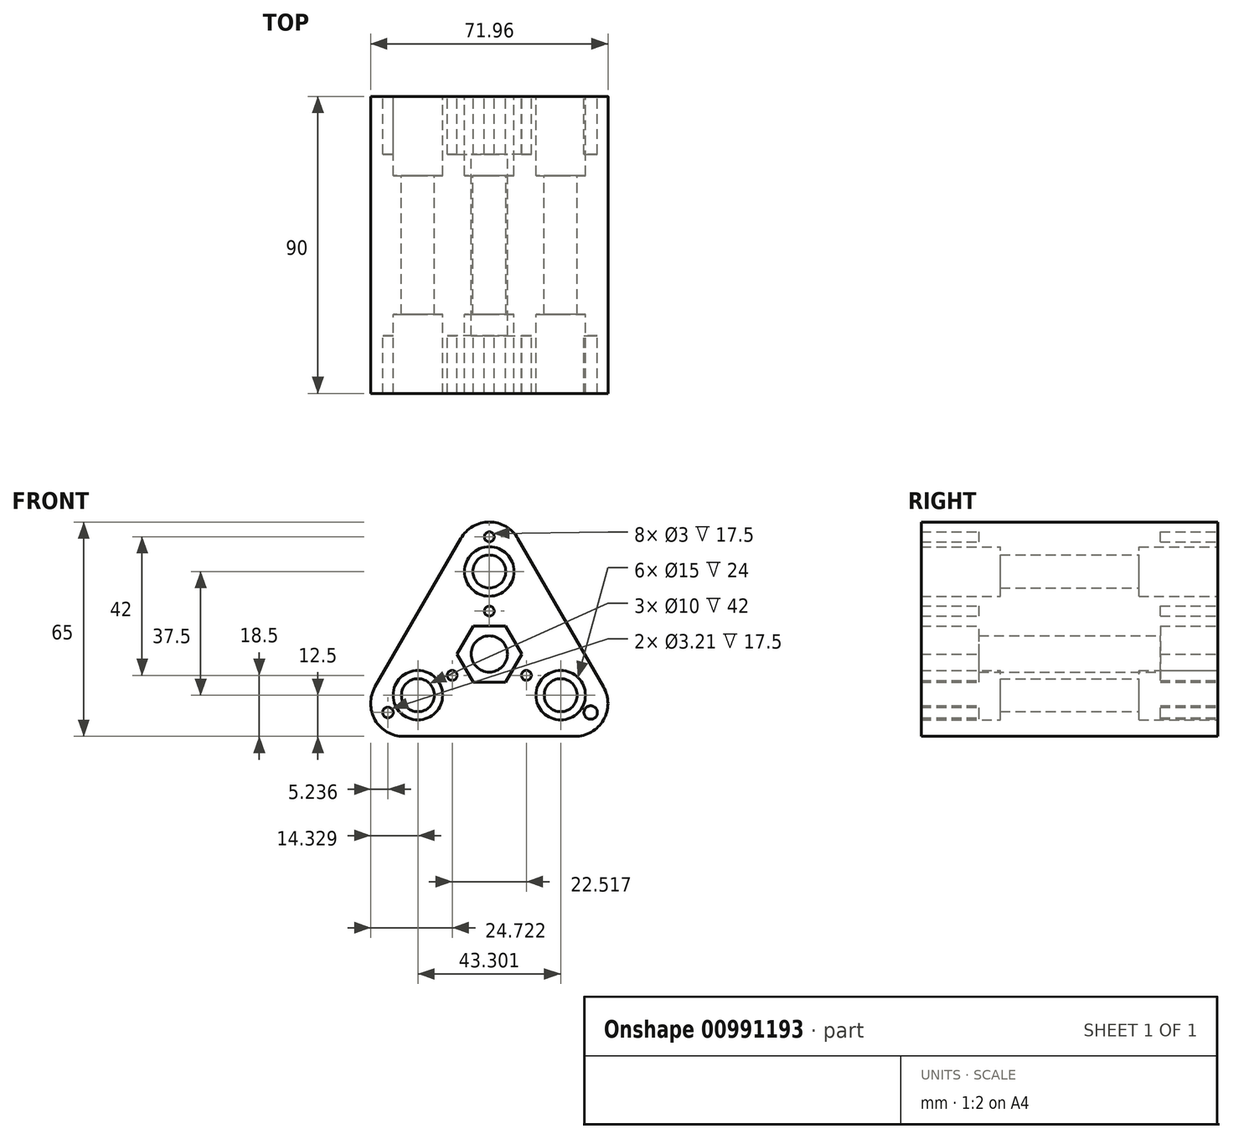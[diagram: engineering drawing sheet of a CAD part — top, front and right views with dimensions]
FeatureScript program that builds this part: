
annotation { "Feature Type Name" : "Feature", "Feature Type Description" : "" }
export const myFeature = defineFeature(function(context is Context, id is Id, definition is map)
    precondition{}
    {
        {
            var Q0;
            Q0=qCreatedBy(makeId("Front.planeOp"),FACE);
            var sketch = newSketch(context, id + "F0", { "sketchPlane" : qUnion([Q0])});
            skCircle(sketch, "E0", {"center": v(0, 0) * mm, "radius": 25 * mm, "construction": true});
            skLineSegment(sketch, "E1.0", {"start": v(0, 25) * mm, "end": v(21.65, -12.5) * mm, "construction": true});
            skLineSegment(sketch, "E1.1", {"start": v(21.65, -12.5) * mm, "end": v(-21.65, -12.5) * mm, "construction": true});
            skLineSegment(sketch, "E1.2", {"start": v(-21.65, -12.5) * mm, "end": v(0, 25) * mm, "construction": true});
            skCircle(sketch, "E2", {"center": v(0, 25) * mm, "radius": 7.5 * mm});
            skCircle(sketch, "E3", {"center": v(21.65, -12.5) * mm, "radius": 7.5 * mm});
            skCircle(sketch, "E4", {"center": v(-21.65, -12.5) * mm, "radius": 7.5 * mm});
            skCircle(sketch, "E5", {"center": v(0, 0) * mm, "radius": 9.81 * mm, "construction": true});
            skCircle(sketch, "E6", {"center": v(-21.65, -12.5) * mm, "radius": 5 * mm});
            skCircle(sketch, "E7", {"center": v(0, 25) * mm, "radius": 5 * mm});
            skCircle(sketch, "E8", {"center": v(21.65, -12.5) * mm, "radius": 5 * mm});
            skLineSegment(sketch, "E9.0", {"start": v(-9.81, 0) * mm, "end": v(-4.9, 8.5) * mm});
            skLineSegment(sketch, "E9.1", {"start": v(-4.9, 8.5) * mm, "end": v(4.9, 8.5) * mm});
            skLineSegment(sketch, "E9.2", {"start": v(4.9, 8.5) * mm, "end": v(9.82, 0) * mm});
            skLineSegment(sketch, "E9.3", {"start": v(9.81, 0) * mm, "end": v(4.9, -8.5) * mm});
            skLineSegment(sketch, "E9.4", {"start": v(4.9, -8.5) * mm, "end": v(-4.9, -8.5) * mm});
            skLineSegment(sketch, "E9.5", {"start": v(-4.9, -8.5) * mm, "end": v(-9.81, 0) * mm});
            skLineSegment(sketch, "E10.0", {"start": v(25.98, -25) * mm, "end": v(-25.98, -25) * mm});
            skLineSegment(sketch, "E10.1", {"start": v(-34.64, -10) * mm, "end": v(-8.66, 35) * mm});
            skLineSegment(sketch, "E10.2", {"start": v(8.66, 35) * mm, "end": v(34.64, -10) * mm});
            skPoint(sketch, "E10.0.midPoint", {"position": v(0, -25) * mm});
            skPoint(sketch, "E11.visualSharp", {"position": v(0, 50) * mm});
            skArc(sketch, "E11.filletArc", {"start": v(8.66, 35) * mm, "mid": v(0, 40) * mm, "end": v(-8.66, 35) * mm});
            skPoint(sketch, "E12.visualSharp", {"position": v(43.3, -25) * mm});
            skArc(sketch, "E12.filletArc", {"start": v(25.98, -25) * mm, "mid": v(34.64, -20) * mm, "end": v(34.64, -10) * mm});
            skPoint(sketch, "E13.visualSharp", {"position": v(-43.3, -25) * mm});
            skArc(sketch, "E13.filletArc", {"start": v(-34.64, -10) * mm, "mid": v(-34.64, -20) * mm, "end": v(-25.98, -25) * mm});
            skCircle(sketch, "E14", {"center": v(0, 0) * mm, "radius": 5.5 * mm});
            skPoint(sketch, "E15.0.midPoint", {"position": v(0, -10) * mm});
            skPoint(sketch, "E16.visualSharp", {"position": v(17.32, -10) * mm});
            skPoint(sketch, "E17.visualSharp", {"position": v(-17.32, -10) * mm});
            skPoint(sketch, "E18.visualSharp", {"position": v(0, 20) * mm});
            skCircle(sketch, "E19", {"center": v(11.26, -6.5) * mm, "radius": 1.5 * mm});
            skCircle(sketch, "E20", {"center": v(-11.26, -6.5) * mm, "radius": 1.5 * mm});
            skCircle(sketch, "E21", {"center": v(0, 13) * mm, "radius": 1.5 * mm});
            skCircle(sketch, "E22", {"center": v(-30.74, -17.75) * mm, "radius": 1.6 * mm});
            skCircle(sketch, "E23", {"center": v(-30.74, -17.75) * mm, "radius": 3 * mm});
            skLineSegment(sketch, "E24", {"start": v(34.64, -20) * mm, "end": v(21.65, -12.5) * mm, "construction": true});
            skCircle(sketch, "E25", {"center": v(30.74, -17.75) * mm, "radius": 2.03 * mm});
            skCircle(sketch, "E26", {"center": v(30.74, -17.75) * mm, "radius": 3 * mm});
            skCircle(sketch, "E27", {"center": v(11.26, -6.5) * mm, "radius": 3 * mm});
            skCircle(sketch, "E28", {"center": v(-11.26, -6.5) * mm, "radius": 3 * mm});
            skCircle(sketch, "E29", {"center": v(0, 13) * mm, "radius": 3 * mm});
            skCircle(sketch, "E30", {"center": v(0, 35.5) * mm, "radius": 1.5 * mm});
            skCircle(sketch, "E31", {"center": v(0, 35.5) * mm, "radius": 3 * mm});
            skLineSegment(sketch, "E32", {"start": v(-21.65, -12.5) * mm, "end": v(0, 0) * mm, "construction": true});
            skLineSegment(sketch, "E33", {"start": v(0, 0) * mm, "end": v(21.65, -12.5) * mm, "construction": true});
            skLineSegment(sketch, "E34", {"start": v(0, 0) * mm, "end": v(0, 25) * mm, "construction": true});
            skLineSegment(sketch, "E35", {"start": v(0, 40) * mm, "end": v(0, 25) * mm, "construction": true});
            skLineSegment(sketch, "E36", {"start": v(-34.64, -20) * mm, "end": v(-21.65, -12.5) * mm, "construction": true});
            skSolve(sketch);
        }
        {
            var Q0;
            Q0=makeQuery(id+"F0.imprint","IMPRINT",FACE,{"disambiguationData":[TD([[makeQuery(id+"F0.imprint","IMPRINT",EDGE,{"derivedFrom":sQuery(id+"F0.wireOp",EDGE,"E2")}),-1.0]])]});
            var Q1;
            Q1=makeQuery(id+"F0.imprint","IMPRINT",FACE,{"disambiguationData":[TD([[makeQuery(id+"F0.imprint","IMPRINT",EDGE,{"derivedFrom":sQuery(id+"F0.wireOp",EDGE,"E9.0")}),-1.0]])]});
            var Q2;
            Q2=makeQuery(id+"F0.imprint","IMPRINT",FACE,{"disambiguationData":[TD([[makeQuery(id+"F0.imprint","IMPRINT",EDGE,{"derivedFrom":sQuery(id+"F0.wireOp",EDGE,"E4")}),1.0]])]});
            var Q3;
            Q3=makeQuery(id+"F0.imprint","IMPRINT",FACE,{"disambiguationData":[TD([[makeQuery(id+"F0.imprint","IMPRINT",EDGE,{"derivedFrom":sQuery(id+"F0.wireOp",EDGE,"E3")}),1.0]])]});
            var Q4;
            Q4=makeQuery(id+"F0.imprint","IMPRINT",FACE,{"disambiguationData":[TD([[makeQuery(id+"F0.imprint","IMPRINT",EDGE,{"derivedFrom":sQuery(id+"F0.wireOp",EDGE,"E2")}),1.0]])]});
            var Q5;
            Q5=makeQuery(id+"F0.imprint","IMPRINT",FACE,{"disambiguationData":[TD([[makeQuery(id+"F0.imprint","IMPRINT",EDGE,{"derivedFrom":sQuery(id+"F0.wireOp",EDGE,"E9.0")}),1.0]])]});
            var Q6;
            Q6=makeQuery(id+"F0.imprint","IMPRINT",FACE,{"disambiguationData":[TD([[makeQuery(id+"F0.imprint","IMPRINT",EDGE,{"derivedFrom":sQuery(id+"F0.wireOp",EDGE,"E21")}),1.0]])]});
            var Q7;
            Q7=makeQuery(id+"F0.imprint","IMPRINT",FACE,{"disambiguationData":[TD([[makeQuery(id+"F0.imprint","IMPRINT",EDGE,{"derivedFrom":sQuery(id+"F0.wireOp",EDGE,"E20")}),1.0]])]});
            var Q8;
            Q8=makeQuery(id+"F0.imprint","IMPRINT",FACE,{"disambiguationData":[TD([[makeQuery(id+"F0.imprint","IMPRINT",EDGE,{"derivedFrom":sQuery(id+"F0.wireOp",EDGE,"E19")}),1.0]])]});
            var Q9;
            Q9=makeQuery(id+"F0.imprint","IMPRINT",FACE,{"disambiguationData":[TD([[makeQuery(id+"F0.imprint","IMPRINT",EDGE,{"derivedFrom":sQuery(id+"F0.wireOp",EDGE,"E21")}),-1.0]])]});
            var Q10;
            Q10=makeQuery(id+"F0.imprint","IMPRINT",FACE,{"disambiguationData":[TD([[makeQuery(id+"F0.imprint","IMPRINT",EDGE,{"derivedFrom":sQuery(id+"F0.wireOp",EDGE,"E20")}),-1.0]])]});
            var Q11;
            Q11=makeQuery(id+"F0.imprint","IMPRINT",FACE,{"disambiguationData":[TD([[makeQuery(id+"F0.imprint","IMPRINT",EDGE,{"derivedFrom":sQuery(id+"F0.wireOp",EDGE,"E19")}),-1.0]])]});
            extrude(context, id + "F1", {"entities" : qUnion([Q0, Q1, Q2, Q3, Q4, Q5, Q6, Q7, Q8, Q9, Q10, Q11]), "depth" : 42 * mm, "offsetDistance" : 25 * mm, "symmetric" : true});
        }
        {
            var Q0;
            Q0=makeQuery(id+"F0.imprint","IMPRINT",FACE,{"disambiguationData":[TD([[makeQuery(id+"F0.imprint","IMPRINT",EDGE,{"derivedFrom":sQuery(id+"F0.wireOp",EDGE,"E2")}),-1.0]])]});
            var Q1;
            Q1=makeQuery(id+"F0.imprint","IMPRINT",FACE,{"disambiguationData":[TD([[makeQuery(id+"F0.imprint","IMPRINT",EDGE,{"derivedFrom":sQuery(id+"F0.wireOp",EDGE,"E25")}),-1.0]])]});
            var Q2;
            Q2=makeQuery(id+"F0.imprint","IMPRINT",FACE,{"disambiguationData":[TD([[makeQuery(id+"F0.imprint","IMPRINT",EDGE,{"derivedFrom":sQuery(id+"F0.wireOp",EDGE,"E22")}),-1.0]])]});
            var Q3;
            Q3=makeQuery(id+"F0.imprint","IMPRINT",FACE,{"disambiguationData":[TD([[makeQuery(id+"F0.imprint","IMPRINT",EDGE,{"derivedFrom":sQuery(id+"F0.wireOp",EDGE,"E30")}),-1.0]])]});
            var Q4;
            Q4=makeQuery(id+"F0.imprint","IMPRINT",FACE,{"disambiguationData":[TD([[makeQuery(id+"F0.imprint","IMPRINT",EDGE,{"derivedFrom":sQuery(id+"F0.wireOp",EDGE,"E21")}),-1.0]])]});
            var Q5;
            Q5=makeQuery(id+"F0.imprint","IMPRINT",FACE,{"disambiguationData":[TD([[makeQuery(id+"F0.imprint","IMPRINT",EDGE,{"derivedFrom":sQuery(id+"F0.wireOp",EDGE,"E21")}),1.0]])]});
            var Q6;
            Q6=makeQuery(id+"F0.imprint","IMPRINT",FACE,{"disambiguationData":[TD([[makeQuery(id+"F0.imprint","IMPRINT",EDGE,{"derivedFrom":sQuery(id+"F0.wireOp",EDGE,"E19")}),-1.0]])]});
            var Q7;
            Q7=makeQuery(id+"F0.imprint","IMPRINT",FACE,{"disambiguationData":[TD([[makeQuery(id+"F0.imprint","IMPRINT",EDGE,{"derivedFrom":sQuery(id+"F0.wireOp",EDGE,"E19")}),1.0]])]});
            var Q8;
            Q8=makeQuery(id+"F0.imprint","IMPRINT",FACE,{"disambiguationData":[TD([[makeQuery(id+"F0.imprint","IMPRINT",EDGE,{"derivedFrom":sQuery(id+"F0.wireOp",EDGE,"E20")}),-1.0]])]});
            var Q9;
            Q9=makeQuery(id+"F0.imprint","IMPRINT",FACE,{"disambiguationData":[TD([[makeQuery(id+"F0.imprint","IMPRINT",EDGE,{"derivedFrom":sQuery(id+"F0.wireOp",EDGE,"E20")}),1.0]])]});
            var Q10;
            Q10=makeQuery(id+"F0.imprint","IMPRINT",FACE,{"disambiguationData":[TD([[makeQuery(id+"F0.imprint","IMPRINT",EDGE,{"derivedFrom":sQuery(id+"F0.wireOp",EDGE,"E9.0")}),-1.0]])]});
            var Q11;
            Q11=makeQuery(id+"F0.imprint","IMPRINT",FACE,{"disambiguationData":[TD([[makeQuery(id+"F0.imprint","IMPRINT",EDGE,{"derivedFrom":sQuery(id+"F0.wireOp",EDGE,"E30")}),1.0]])]});
            var Q12;
            Q12=makeQuery(id+"F0.imprint","IMPRINT",FACE,{"disambiguationData":[TD([[makeQuery(id+"F0.imprint","IMPRINT",EDGE,{"derivedFrom":sQuery(id+"F0.wireOp",EDGE,"E25")}),1.0]])]});
            var Q13;
            Q13=makeQuery(id+"F0.imprint","IMPRINT",FACE,{"disambiguationData":[TD([[makeQuery(id+"F0.imprint","IMPRINT",EDGE,{"derivedFrom":sQuery(id+"F0.wireOp",EDGE,"E22")}),1.0]])]});
            extrude(context, id + "F2", {"entities" : qUnion([Q0, Q1, Q2, Q3, Q4, Q5, Q6, Q7, Q8, Q9, Q10, Q11, Q12, Q13]), "operationType" : NewBodyOperationType.ADD, "depth" : 55 * mm, "offsetDistance" : 25 * mm, "symmetric" : true});
        }
        {
            var Q0;
            Q0=makeQuery(id+"F0.imprint","IMPRINT",FACE,{"disambiguationData":[TD([[makeQuery(id+"F0.imprint","IMPRINT",EDGE,{"derivedFrom":sQuery(id+"F0.wireOp",EDGE,"E2")}),-1.0]])]});
            var Q1;
            Q1=makeQuery(id+"F0.imprint","IMPRINT",FACE,{"disambiguationData":[TD([[makeQuery(id+"F0.imprint","IMPRINT",EDGE,{"derivedFrom":sQuery(id+"F0.wireOp",EDGE,"E25")}),-1.0]])]});
            var Q2;
            Q2=makeQuery(id+"F0.imprint","IMPRINT",FACE,{"disambiguationData":[TD([[makeQuery(id+"F0.imprint","IMPRINT",EDGE,{"derivedFrom":sQuery(id+"F0.wireOp",EDGE,"E22")}),-1.0]])]});
            var Q3;
            Q3=makeQuery(id+"F0.imprint","IMPRINT",FACE,{"disambiguationData":[TD([[makeQuery(id+"F0.imprint","IMPRINT",EDGE,{"derivedFrom":sQuery(id+"F0.wireOp",EDGE,"E30")}),-1.0]])]});
            var Q4;
            Q4=makeQuery(id+"F0.imprint","IMPRINT",FACE,{"disambiguationData":[TD([[makeQuery(id+"F0.imprint","IMPRINT",EDGE,{"derivedFrom":sQuery(id+"F0.wireOp",EDGE,"E21")}),-1.0]])]});
            var Q5;
            Q5=makeQuery(id+"F0.imprint","IMPRINT",FACE,{"disambiguationData":[TD([[makeQuery(id+"F0.imprint","IMPRINT",EDGE,{"derivedFrom":sQuery(id+"F0.wireOp",EDGE,"E19")}),-1.0]])]});
            var Q6;
            Q6=makeQuery(id+"F0.imprint","IMPRINT",FACE,{"disambiguationData":[TD([[makeQuery(id+"F0.imprint","IMPRINT",EDGE,{"derivedFrom":sQuery(id+"F0.wireOp",EDGE,"E20")}),-1.0]])]});
            extrude(context, id + "F3", {"entities" : qUnion([Q0, Q1, Q2, Q3, Q4, Q5, Q6]), "operationType" : NewBodyOperationType.ADD, "depth" : 90 * mm, "offsetDistance" : 25 * mm, "symmetric" : true});
        }
    });
